# Revit family: LUNA II W-BSN-BTH MXR 220
name_source: partatom
category: Plumbing Fixtures
units: mm (PartAtom-declared; Revit-internal decimal feet)

## family parameters
Cut with Voids When Loaded = Yes
Host = Face
OmniClass Number = 23.45.55.17
OmniClass Title = Mixing Faucets
Part Type = Normal
Room Calculation Point = No
Round Connector Dimension = Use Diameter
Shared = No

## types (4) — shared parameters
Assembly Code = D2020300
CW Connection = Yes
HW Connection = Yes
Manufacturer = GWA Bathrooms & Kitchens
URL = https://www.caroma.com.au
Vent Connection = No
Waste Connection = No
zero-valued in all types: Default Elevation

## per-type parameters (varying)
| type | Base_Material | Model |
| LUNA II W-BSN-BTH MXR 220 CH LF | GWA_Metal-Chrome | 68204C6AF |
| LUNA II W-BSN-BTH MXR 220 BL LF | GWA-Metal-Black | 68204BL6AF |
| LUNA II W-BSN-BTH MXR 220 BB LF | GWA_Metal-Brushed-Brass | 68204BB6AF |
| LUNA II W-BSN-BTH MXR 220 BN LF | GWA_Metal-Brushed-Nickel | 68204BN6AF |

note: column(s) folded — value = type name in every type: Description

## geometry (parser evidence)
native form markers: Sweep x2
no freeform markers — native parametric forms only
